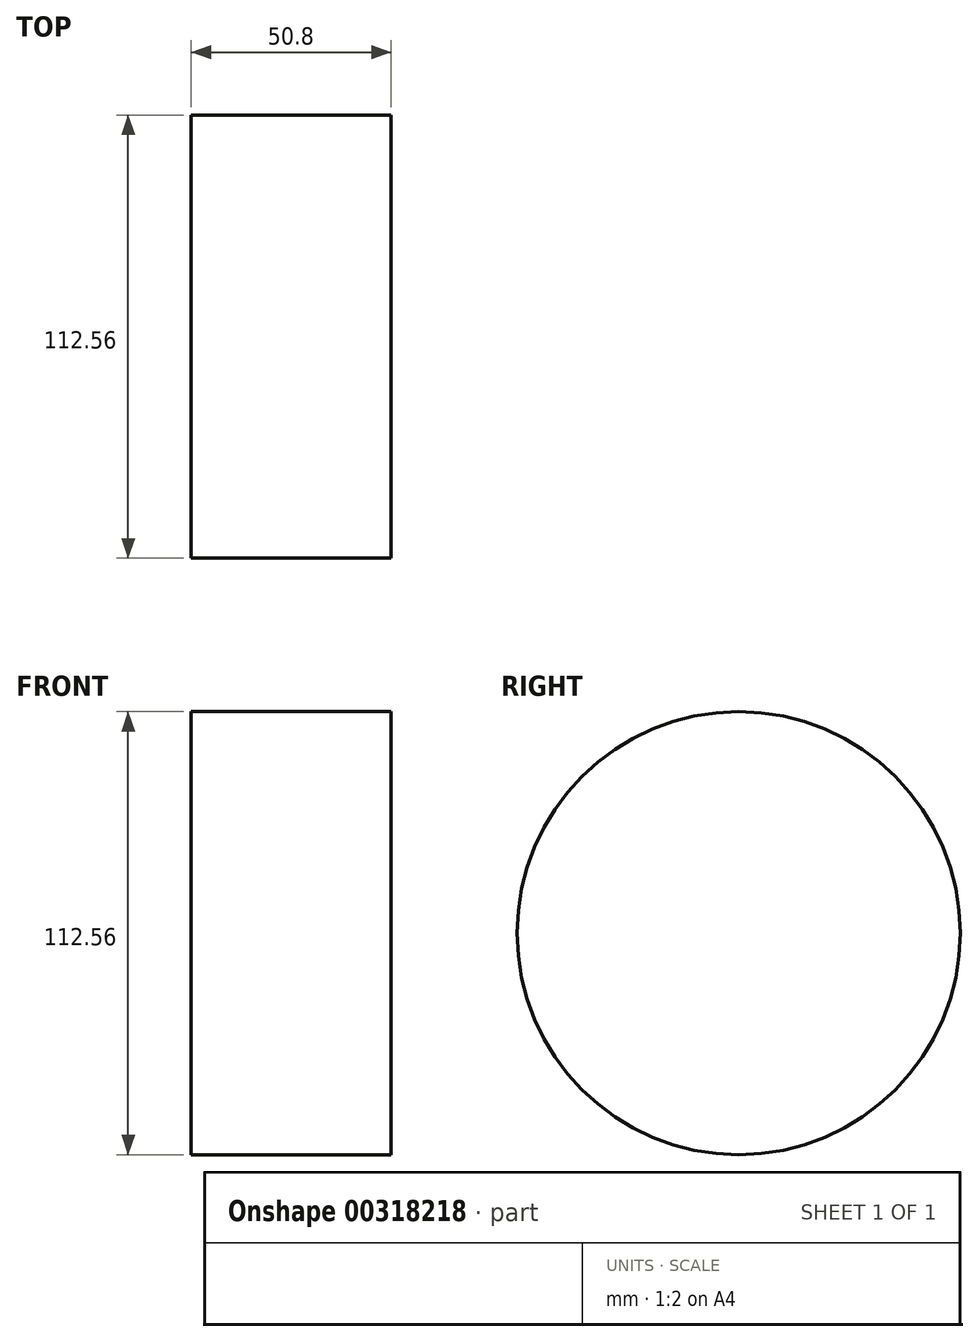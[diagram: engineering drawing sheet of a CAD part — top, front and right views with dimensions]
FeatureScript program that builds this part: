
annotation { "Feature Type Name" : "Feature", "Feature Type Description" : "" }
export const myFeature = defineFeature(function(context is Context, id is Id, definition is map)
    precondition{}
    {
        {
            var Q0;
            Q0=qCreatedBy(makeId("Right.planeOp"),FACE);
            var sketch = newSketch(context, id + "F0", { "sketchPlane" : qUnion([Q0])});
            skCircle(sketch, "E0", {"center": v(-14.69, 29.96) * mm, "radius": 56.28 * mm});
            skSolve(sketch);
        }
        {
            var Q0;
            Q0 = qSketchRegion(id + "F0", true);
            extrude(context, id + "F1", {"entities" : qUnion([Q0]), "depth" : 50.8 * mm});
        }
    });
